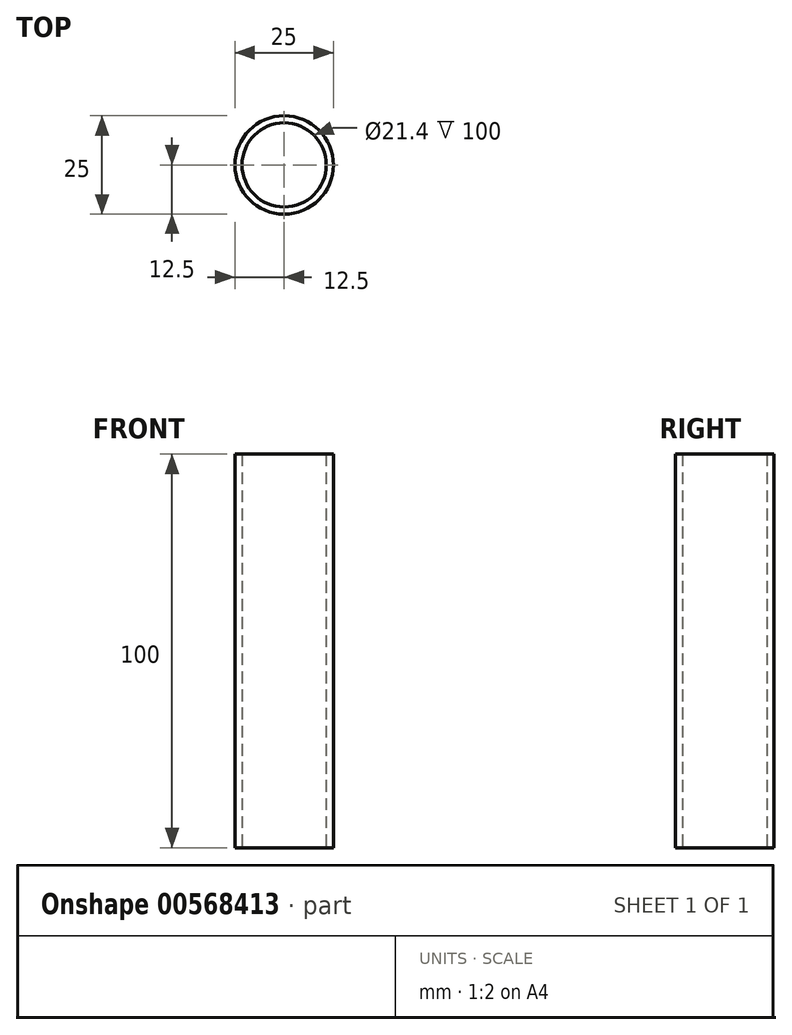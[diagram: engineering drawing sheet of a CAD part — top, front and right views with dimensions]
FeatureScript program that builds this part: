
annotation { "Feature Type Name" : "Feature", "Feature Type Description" : "" }
export const myFeature = defineFeature(function(context is Context, id is Id, definition is map)
    precondition{}
    {
        {
            var Q0;
            Q0=qCreatedBy(makeId("Top.planeOp"),FACE);
            var sketch = newSketch(context, id + "F0", { "sketchPlane" : qUnion([Q0])});
            skCircle(sketch, "E0", {"center": v(0, 0) * mm, "radius": 12.5 * mm});
            skCircle(sketch, "E1.0", {"center": v(0, 0) * mm, "radius": 10.7 * mm});
            skSolve(sketch);
        }
        {
            var Q0;
            Q0=makeQuery(id+"F0.imprint","IMPRINT",FACE,{"disambiguationData":[TD([[makeQuery(id+"F0.imprint","IMPRINT",EDGE,{"derivedFrom":sQuery(id+"F0.wireOp",EDGE,"E0")}),1.0]])]});
            extrude(context, id + "F1", {"entities" : qUnion([Q0]), "depth" : 100 * mm, "offsetDistance" : 25 * mm});
        }
    });
